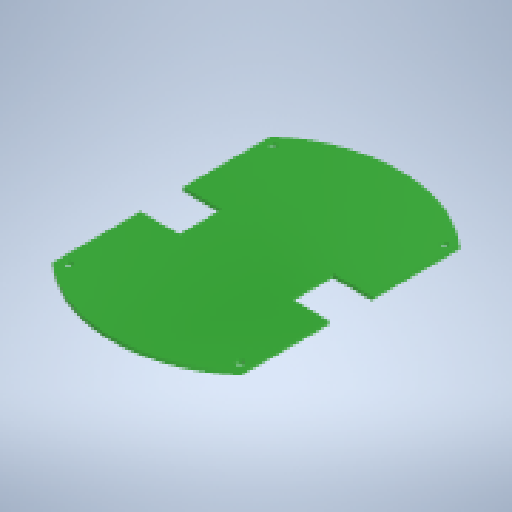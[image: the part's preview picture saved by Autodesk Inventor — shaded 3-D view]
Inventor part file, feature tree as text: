
AUTODESK INVENTOR PART (.ipt)
format: ipt  version: 2025.3 (Build 293356000, 356)  size: 258,560 bytes
history: native  units: mm
features: sketch x3, extrude x2, other x1, hole x1, fillet x1
ambient origin geometry x8: Origin, YZ Plane, XZ Plane, XY Plane, X Axis, Y Axis, Z Axis, Center Point
bodies: Body1 (feature_tree)
feature tree (8):
  other  "ソリッド1"
  extrude  "基板"  Depth=130.0mm
  hole  "スペーサ取付穴"  [1 undecoded]
  extrude  "モータ用切欠き"  Depth=1.6mm TaperAngle=0.0deg
  fillet  "フィレット1"  Radius=4.0mm
  sketch  "スケッチ1"
  sketch  "スケッチ4"
  sketch  "スケッチ6"
note: 1 required parameter value undecoded (feature->parameter linkage not recoverable at this tier; creation-order binding heuristic only, values carry confidence <= 0.55)
